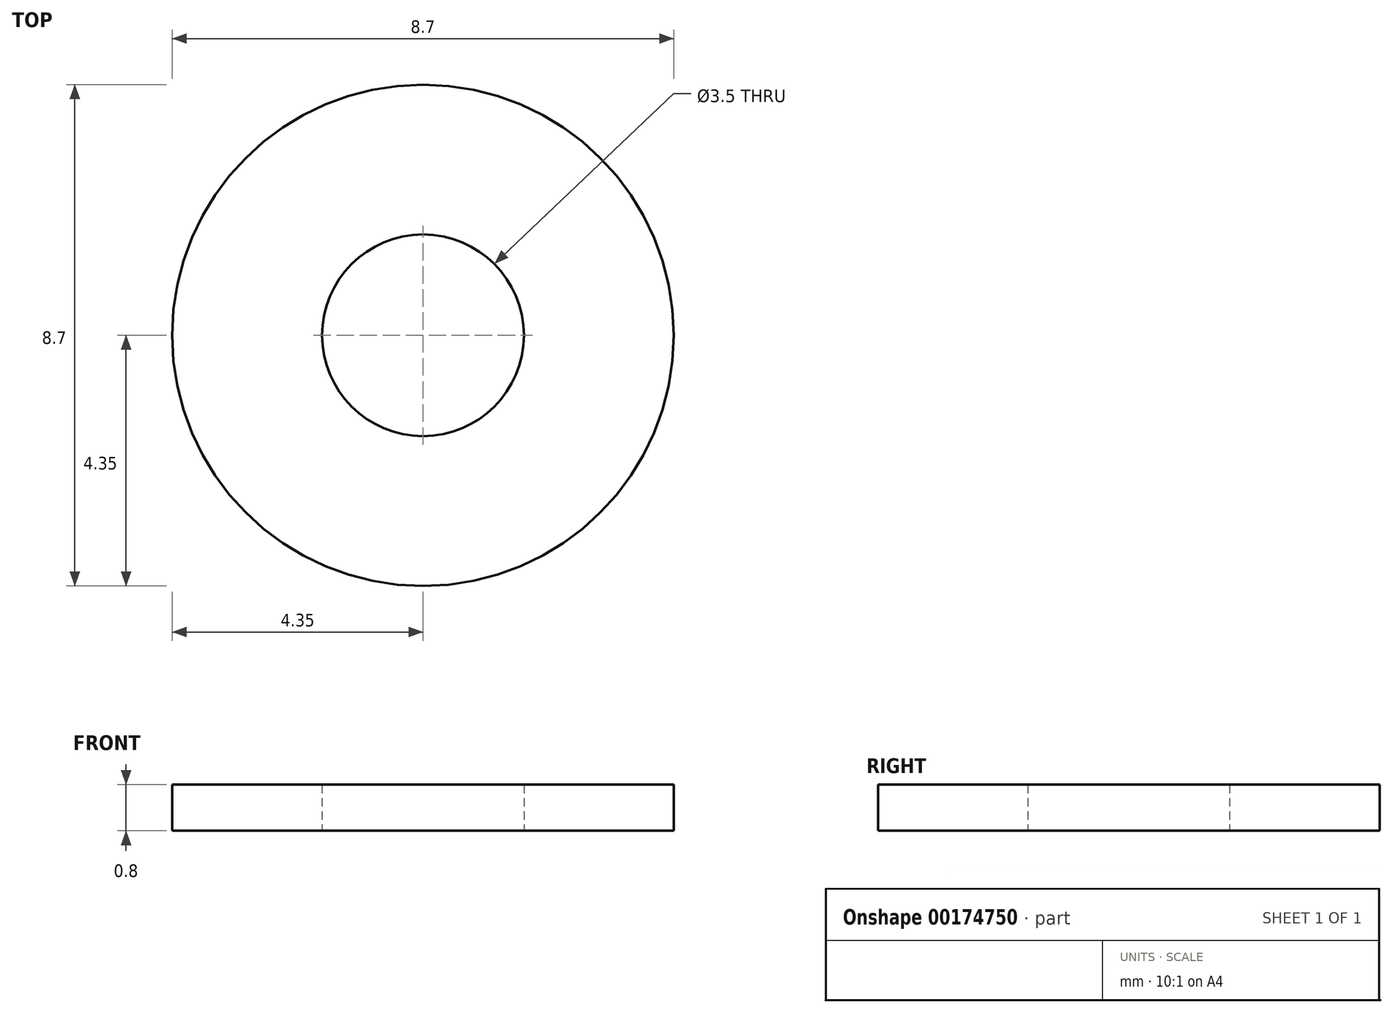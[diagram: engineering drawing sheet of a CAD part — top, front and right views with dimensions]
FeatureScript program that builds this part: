
annotation { "Feature Type Name" : "Feature", "Feature Type Description" : "" }
export const myFeature = defineFeature(function(context is Context, id is Id, definition is map)
    precondition{}
    {
        {
            var Q0;
            Q0=qCreatedBy(makeId("Top.planeOp"),FACE);
            var sketch = newSketch(context, id + "F0", { "sketchPlane" : qUnion([Q0])});
            skCircle(sketch, "E0", {"center": v(0, 0) * mm, "radius": 4.35 * mm});
            skCircle(sketch, "E1", {"center": v(0, 0) * mm, "radius": 1.75 * mm});
            skSolve(sketch);
        }
        {
            var Q0;
            Q0 = qSketchRegion(id + "F0", true);
            extrude(context, id + "F1", {"entities" : qUnion([Q0]), "depth" : 0.8 * mm});
        }
    });
